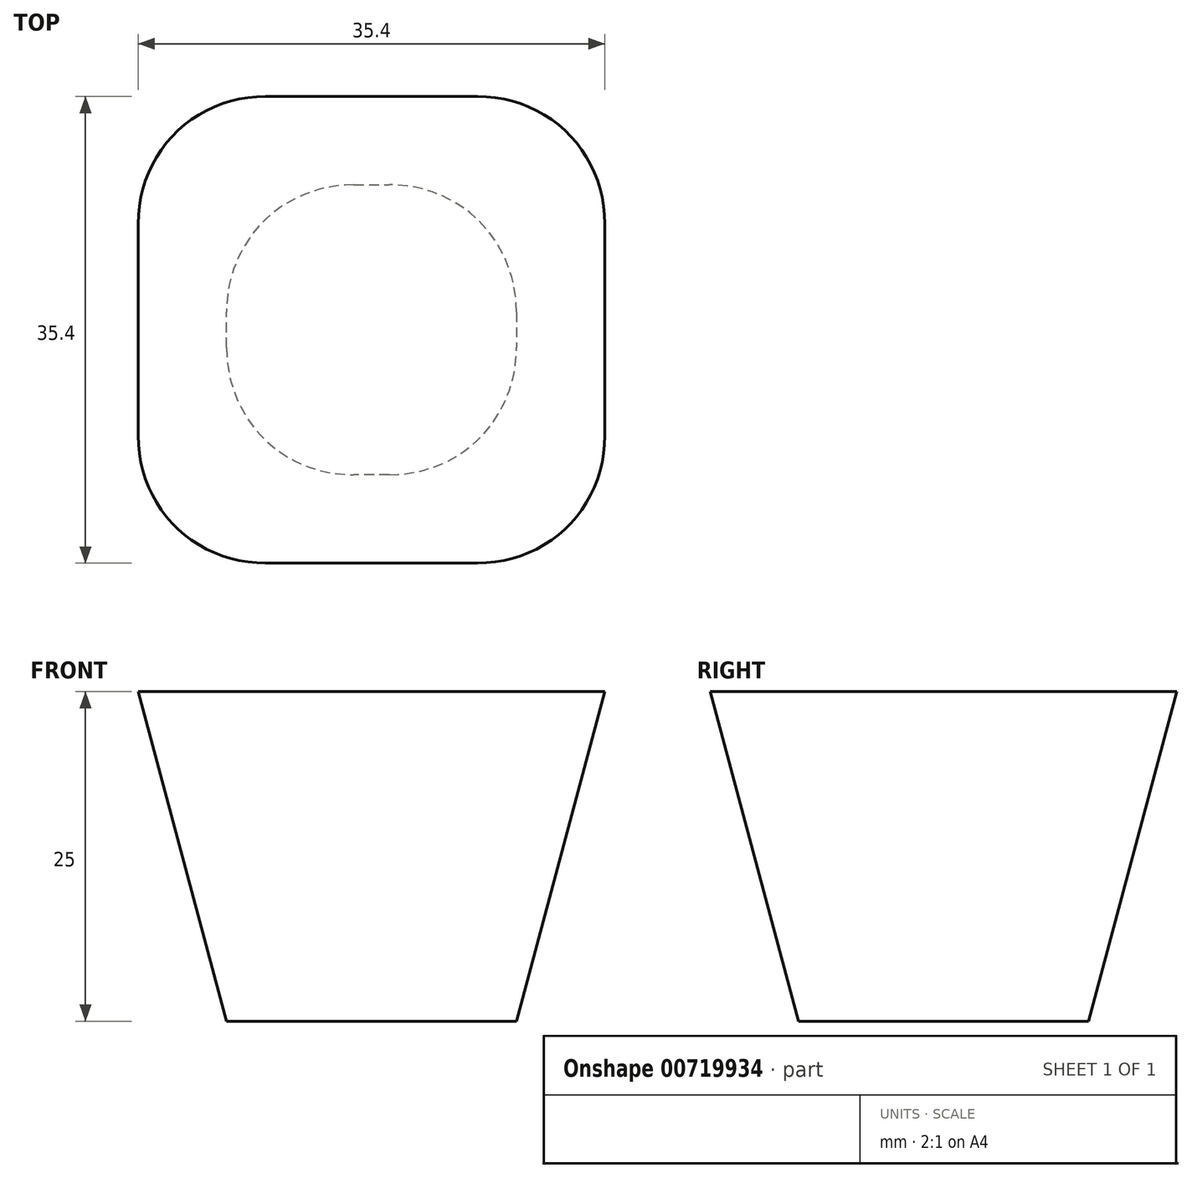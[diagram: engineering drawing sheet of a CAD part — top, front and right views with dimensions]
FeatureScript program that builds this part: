
annotation { "Feature Type Name" : "Feature", "Feature Type Description" : "" }
export const myFeature = defineFeature(function(context is Context, id is Id, definition is map)
    precondition{}
    {
        {
            var Q0;
            Q0=qCreatedBy(makeId("Top.planeOp"),FACE);
            var sketch = newSketch(context, id + "F0", { "sketchPlane" : qUnion([Q0])});
            skLineSegment(sketch, "E0.bottom", {"start": v(11, 11) * mm, "end": v(-11, 11) * mm});
            skLineSegment(sketch, "E0.top", {"start": v(11, -11) * mm, "end": v(-11, -11) * mm});
            skLineSegment(sketch, "E0.left", {"start": v(11, 11) * mm, "end": v(11, -11) * mm});
            skLineSegment(sketch, "E0.right", {"start": v(-11, 11) * mm, "end": v(-11, -11) * mm});
            skSolve(sketch);
        }
        {
            var Q0;
            Q0=makeQuery(id+"F0.imprint","IMPRINT",FACE,{"disambiguationData":[TD([[makeQuery(id+"F0.imprint","IMPRINT",EDGE,{"derivedFrom":sQuery(id+"F0.wireOp",EDGE,"E0.bottom")}),1.0]])]});
            extrude(context, id + "F1", {"entities" : qUnion([Q0]), "depth" : 25 * mm, "offsetDistance" : 25 * mm, "hasDraft" : true, "draftAngle" : 15 * degree});
        }
        {
            var Q0;
            Q0=makeQuery(id+"F1.opExtrude","SWEPT_EDGE",EDGE,{"disambiguationData":[OSD([sQuery(id+"F0.wireOp",EDGE,"E0.top"),sQuery(id+"F0.wireOp",EDGE,"E0.right")])]});
            var Q1;
            Q1=makeQuery(id+"F1.opExtrude","SWEPT_EDGE",EDGE,{"disambiguationData":[OSD([sQuery(id+"F0.wireOp",EDGE,"E0.bottom"),sQuery(id+"F0.wireOp",EDGE,"E0.right")])]});
            var Q2;
            Q2=makeQuery(id+"F1.opExtrude","SWEPT_EDGE",EDGE,{"disambiguationData":[OSD([sQuery(id+"F0.wireOp",EDGE,"E0.bottom"),sQuery(id+"F0.wireOp",EDGE,"E0.left")])]});
            var Q3;
            Q3=makeQuery(id+"F1.opExtrude","SWEPT_EDGE",EDGE,{"disambiguationData":[OSD([sQuery(id+"F0.wireOp",EDGE,"E0.top"),sQuery(id+"F0.wireOp",EDGE,"E0.left")])]});
            fillet(context, id + "F2", {"entities" : qUnion([Q0, Q1, Q2, Q3]), "radius" : 10 * mm, "tangentPropagation" : true, "allowEdgeOverflow" : false});
        }
    });
